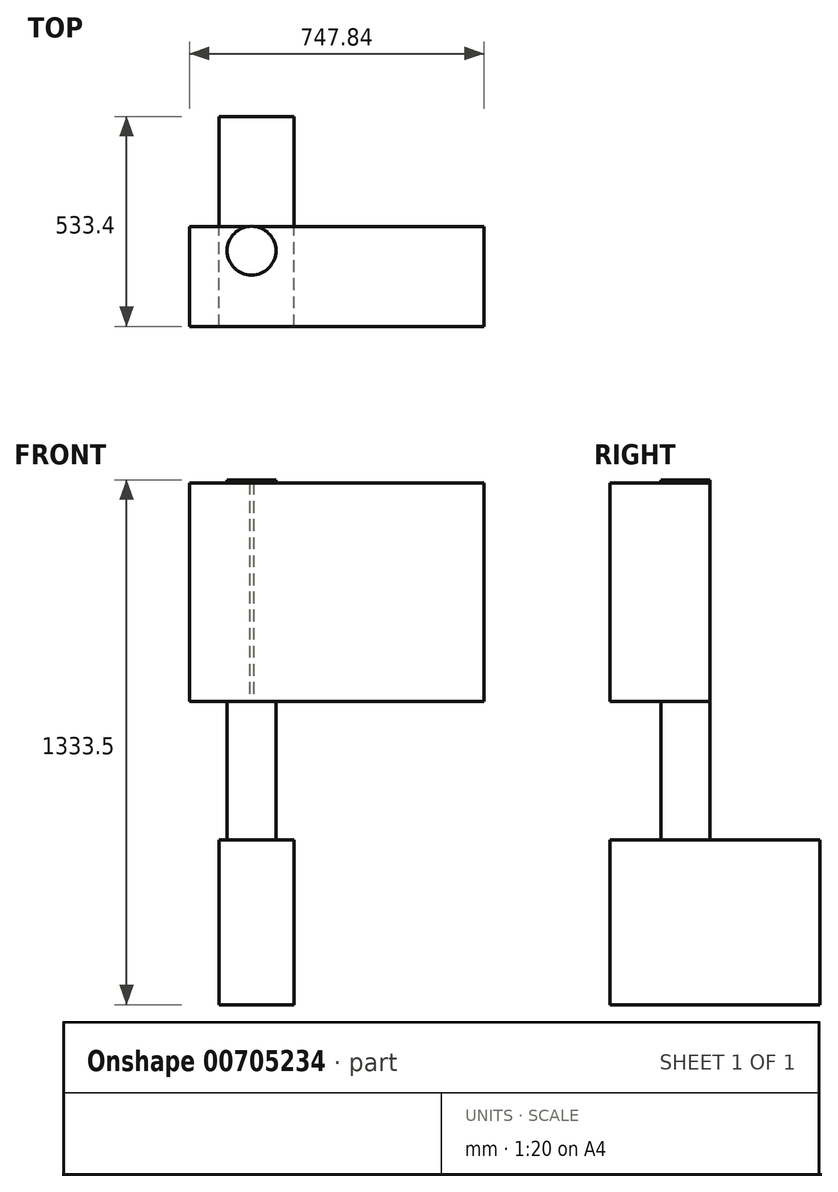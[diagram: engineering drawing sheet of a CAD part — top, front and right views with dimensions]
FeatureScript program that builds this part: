
annotation { "Feature Type Name" : "Feature", "Feature Type Description" : "" }
export const myFeature = defineFeature(function(context is Context, id is Id, definition is map)
    precondition{}
    {
        {
            var Q0;
            Q0=qCreatedBy(makeId("Top.planeOp"),FACE);
            var sketch = newSketch(context, id + "F0", { "sketchPlane" : qUnion([Q0])});
            skLineSegment(sketch, "E0.bottom", {"start": v(0, 0) * mm, "end": v(190.5, 0) * mm});
            skLineSegment(sketch, "E0.top", {"start": v(0, 533.4) * mm, "end": v(190.5, 533.4) * mm});
            skLineSegment(sketch, "E0.left", {"start": v(0, 0) * mm, "end": v(0, 533.4) * mm});
            skLineSegment(sketch, "E0.right", {"start": v(190.5, 0) * mm, "end": v(190.5, 533.4) * mm});
            skSolve(sketch);
        }
        {
            var Q0;
            Q0=makeQuery(id+"F0.imprint","IMPRINT",FACE,{"disambiguationData":[TD([[makeQuery(id+"F0.imprint","IMPRINT",EDGE,{"derivedFrom":sQuery(id+"F0.wireOp",EDGE,"E0.bottom")}),1.0]])]});
            extrude(context, id + "F1", {"entities" : qUnion([Q0]), "depth" : 419.1 * mm, "offsetDistance" : 25.4 * mm});
        }
        {
            var Q0;
            Q0=makeQuery(id+"F1.opExtrude","CAP_FACE",FACE,{"disambiguationData":[OSD([sQuery(id+"F0.wireOp",EDGE,"E0.bottom"),sQuery(id+"F0.wireOp",EDGE,"E0.top"),sQuery(id+"F0.wireOp",EDGE,"E0.left"),sQuery(id+"F0.wireOp",EDGE,"E0.right")])],"isStart":false});
            var sketch = newSketch(context, id + "F2", { "sketchPlane" : qUnion([Q0])});
            skCircle(sketch, "E1", {"center": v(82.93, 192.24) * mm, "radius": 61.95 * mm});
            skSolve(sketch);
        }
        {
            var Q0;
            Q0=makeQuery(id+"F2.imprint","IMPRINT",FACE,{"disambiguationData":[TD([[makeQuery(id+"F2.imprint","IMPRINT",EDGE,{"derivedFrom":sQuery(id+"F2.wireOp",EDGE,"E1")}),1.0]])]});
            extrude(context, id + "F3", {"entities" : qUnion([Q0]), "operationType" : NewBodyOperationType.ADD, "depth" : 914.4 * mm, "offsetDistance" : 25.4 * mm});
        }
        {
            var Q0;
            Q0=makeQuery(id+"F1.opExtrude","SWEPT_FACE",FACE,{"disambiguationData":[OSD([sQuery(id+"F0.wireOp",EDGE,"E0.bottom")])]});
            var sketch = newSketch(context, id + "F4", { "sketchPlane" : qUnion([Q0])});
            skLineSegment(sketch, "E2.bottom", {"start": v(-74.5, 1325.6) * mm, "end": v(673.34, 1325.6) * mm});
            skLineSegment(sketch, "E2.top", {"start": v(-74.5, 770.25) * mm, "end": v(673.34, 770.25) * mm});
            skLineSegment(sketch, "E2.left", {"start": v(-74.5, 1325.6) * mm, "end": v(-74.5, 770.25) * mm});
            skLineSegment(sketch, "E2.right", {"start": v(673.34, 1325.6) * mm, "end": v(673.34, 770.25) * mm});
            skSolve(sketch);
        }
        {
            var Q0;
            Q0=makeQuery(id+"F4.imprint","IMPRINT",FACE,{"disambiguationData":[TD([[makeQuery(id+"F4.imprint","IMPRINT",EDGE,{"derivedFrom":sQuery(id+"F4.wireOp",EDGE,"E2.bottom")}),-1.0]])]});
            extrude(context, id + "F5", {"entities" : qUnion([Q0]), "operationType" : NewBodyOperationType.ADD, "oppositeDirection" : true, "depth" : 254 * mm, "offsetDistance" : 25.4 * mm});
        }
    });
